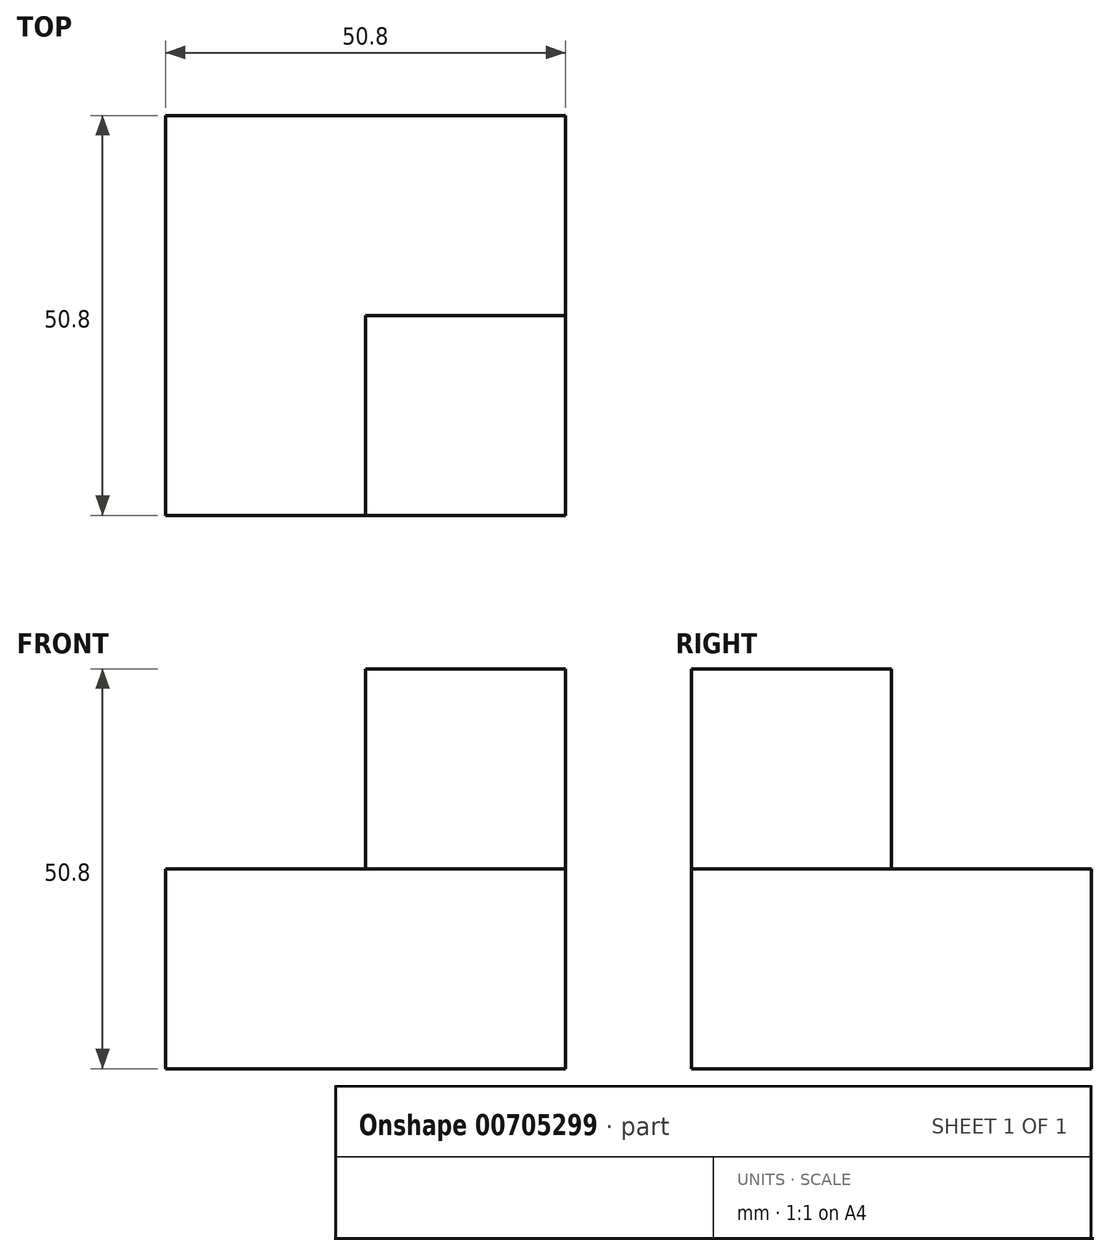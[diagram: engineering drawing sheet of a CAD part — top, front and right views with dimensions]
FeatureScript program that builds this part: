
annotation { "Feature Type Name" : "Feature", "Feature Type Description" : "" }
export const myFeature = defineFeature(function(context is Context, id is Id, definition is map)
    precondition{}
    {
        {
            var Q0;
            Q0=qCreatedBy(makeId("Front.planeOp"),FACE);
            var sketch = newSketch(context, id + "F0", { "sketchPlane" : qUnion([Q0])});
            skLineSegment(sketch, "E0.bottom", {"start": v(0, 0) * mm, "end": v(-25.4, 0) * mm});
            skLineSegment(sketch, "E0.top", {"start": v(0, 25.4) * mm, "end": v(-25.4, 25.4) * mm});
            skLineSegment(sketch, "E0.left", {"start": v(0, 0) * mm, "end": v(0, 25.4) * mm});
            skLineSegment(sketch, "E0.right", {"start": v(-25.4, 0) * mm, "end": v(-25.4, 25.4) * mm});
            skLineSegment(sketch, "E1.bottom", {"start": v(0, 0) * mm, "end": v(25.4, 0) * mm});
            skLineSegment(sketch, "E1.top", {"start": v(0, 25.4) * mm, "end": v(25.4, 25.4) * mm});
            skLineSegment(sketch, "E1.right", {"start": v(25.4, 0) * mm, "end": v(25.4, 25.4) * mm});
            skLineSegment(sketch, "E2.bottom", {"start": v(-25.4, 25.4) * mm, "end": v(0, 25.4) * mm});
            skLineSegment(sketch, "E2.top", {"start": v(-25.4, 50.8) * mm, "end": v(0, 50.8) * mm});
            skLineSegment(sketch, "E2.left", {"start": v(-25.4, 25.4) * mm, "end": v(-25.4, 50.8) * mm});
            skLineSegment(sketch, "E2.right", {"start": v(0, 25.4) * mm, "end": v(0, 50.8) * mm});
            skLineSegment(sketch, "E3.top", {"start": v(0, 50.8) * mm, "end": v(25.4, 50.8) * mm});
            skLineSegment(sketch, "E3.right", {"start": v(25.4, 25.4) * mm, "end": v(25.4, 50.8) * mm});
            skSolve(sketch);
        }
        {
            var Q0;
            Q0=makeQuery(id+"F0.imprint","IMPRINT",FACE,{"disambiguationData":[TD([[makeQuery(id+"F0.imprint","IMPRINT",EDGE,{"derivedFrom":sQuery(id+"F0.wireOp",EDGE,"E0.bottom")}),-1.0]])]});
            var Q1;
            Q1=makeQuery(id+"F0.imprint","IMPRINT",FACE,{"disambiguationData":[TD([[makeQuery(id+"F0.imprint","IMPRINT",EDGE,{"derivedFrom":sQuery(id+"F0.wireOp",EDGE,"E1.bottom")}),1.0]])]});
            extrude(context, id + "F1", {"entities" : qUnion([Q0, Q1]), "oppositeDirection" : true, "depth" : 50.8 * mm, "offsetDistance" : 25.4 * mm});
        }
        {
            var Q0;
            Q0=makeQuery(id+"F0.imprint","IMPRINT",FACE,{"disambiguationData":[TD([[makeQuery(id+"F0.imprint","IMPRINT",EDGE,{"derivedFrom":sQuery(id+"F0.wireOp",EDGE,"E2.bottom")}),1.0]])]});
            var Q1;
            Q1=makeQuery(id+"F0.imprint","IMPRINT",FACE,{"disambiguationData":[TD([[makeQuery(id+"F0.imprint","IMPRINT",EDGE,{"derivedFrom":sQuery(id+"F0.wireOp",EDGE,"E1.top")}),1.0]])]});
            extrude(context, id + "F2", {"entities" : qUnion([Q0, Q1]), "oppositeDirection" : true, "depth" : 25.4 * mm, "offsetDistance" : 25.4 * mm});
        }
    });
